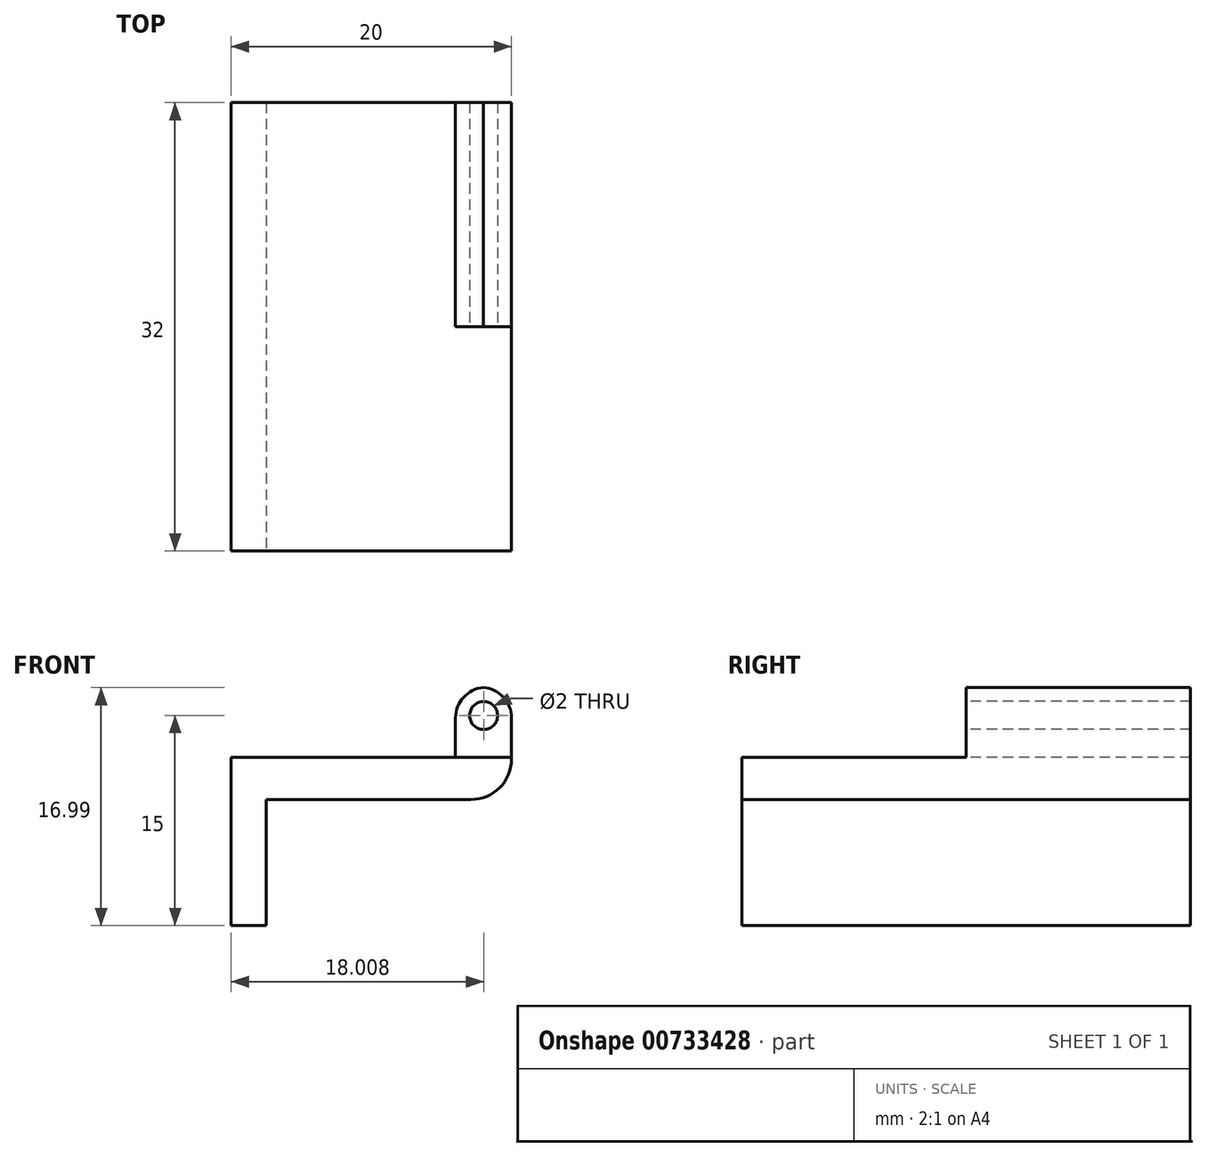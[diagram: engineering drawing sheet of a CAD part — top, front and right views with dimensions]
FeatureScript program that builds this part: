
annotation { "Feature Type Name" : "Feature", "Feature Type Description" : "" }
export const myFeature = defineFeature(function(context is Context, id is Id, definition is map)
    precondition{}
    {
        {
            var Q0;
            Q0=qCreatedBy(makeId("Top.planeOp"),FACE);
            var sketch = newSketch(context, id + "F0", { "sketchPlane" : qUnion([Q0])});
            skLineSegment(sketch, "E0.bottom", {"start": v(0, -16) * mm, "end": v(-20, -16) * mm});
            skLineSegment(sketch, "E0.top", {"start": v(0, 16) * mm, "end": v(-20, 16) * mm});
            skLineSegment(sketch, "E0.left", {"start": v(0, -16) * mm, "end": v(0, 16) * mm});
            skLineSegment(sketch, "E0.right", {"start": v(-20, -16) * mm, "end": v(-20, 16) * mm});
            skSolve(sketch);
        }
        {
            var Q0;
            Q0 = qSketchRegion(id + "F0", true);
            extrude(context, id + "F1", {"entities" : qUnion([Q0]), "depth" : 3 * mm, "offsetDistance" : 25 * mm});
        }
        {
            var Q0;
            Q0=makeQuery(id+"F1.opExtrude","CAP_FACE",FACE,{"disambiguationData":[OSD([sQuery(id+"F0.wireOp",EDGE,"E0.bottom"),sQuery(id+"F0.wireOp",EDGE,"E0.top"),sQuery(id+"F0.wireOp",EDGE,"E0.left"),sQuery(id+"F0.wireOp",EDGE,"E0.right")])],"isStart":true});
            var sketch = newSketch(context, id + "F2", { "sketchPlane" : qUnion([Q0])});
            skLineSegment(sketch, "E1.bottom", {"start": v(-20, -16) * mm, "end": v(-17.5, -16) * mm});
            skLineSegment(sketch, "E1.top", {"start": v(-20, 16) * mm, "end": v(-17.5, 16) * mm});
            skLineSegment(sketch, "E1.left", {"start": v(-20, -16) * mm, "end": v(-20, 16) * mm});
            skLineSegment(sketch, "E1.right", {"start": v(-17.5, -16) * mm, "end": v(-17.5, 16) * mm});
            skSolve(sketch);
        }
        {
            var Q0;
            Q0=makeQuery(id+"F2.imprint","IMPRINT",FACE,{"disambiguationData":[TD([[makeQuery(id+"F2.imprint","IMPRINT",EDGE,{"derivedFrom":sQuery(id+"F2.wireOp",EDGE,"E1.bottom")}),-1.0]])]});
            extrude(context, id + "F3", {"entities" : qUnion([Q0]), "operationType" : NewBodyOperationType.ADD, "depth" : 9 * mm, "offsetDistance" : 25 * mm});
        }
        {
            var Q0;
            Q0=makeQuery(id+"F1.opExtrude","CAP_EDGE",EDGE,{"disambiguationData":[OSD([sQuery(id+"F0.wireOp",EDGE,"E0.left")])],"isStart":true});
            fillet(context, id + "F4", {"entities" : qUnion([Q0]), "radius" : 2.9 * mm, "tangentPropagation" : true, "allowEdgeOverflow" : false});
        }
        {
            var Q0;
            Q0=makeQuery(id+"F1.opExtrude","CAP_FACE",FACE,{"disambiguationData":[OSD([sQuery(id+"F0.wireOp",EDGE,"E0.bottom"),sQuery(id+"F0.wireOp",EDGE,"E0.top"),sQuery(id+"F0.wireOp",EDGE,"E0.left"),sQuery(id+"F0.wireOp",EDGE,"E0.right")])],"isStart":false});
            var sketch = newSketch(context, id + "F5", { "sketchPlane" : qUnion([Q0])});
            skLineSegment(sketch, "E2.bottom", {"start": v(0, 16) * mm, "end": v(0, 16) * mm});
            skLineSegment(sketch, "E2.top", {"start": v(0, 0) * mm, "end": v(0, 0) * mm});
            skLineSegment(sketch, "E2.left", {"start": v(0, 16) * mm, "end": v(0, 0) * mm});
            skLineSegment(sketch, "E2.right", {"start": v(0, 16) * mm, "end": v(0, 0) * mm});
            skLineSegment(sketch, "E3.bottom", {"start": v(0, 16) * mm, "end": v(-4, 16) * mm});
            skLineSegment(sketch, "E3.top", {"start": v(0, 0) * mm, "end": v(-4, 0) * mm});
            skLineSegment(sketch, "E3.right", {"start": v(-4, 16) * mm, "end": v(-4, 0) * mm});
            skSolve(sketch);
        }
        {
            var Q0;
            Q0=makeQuery(id+"F5.imprint","IMPRINT",FACE,{"disambiguationData":[TD([[makeQuery(id+"F5.imprint","IMPRINT",EDGE,{"derivedFrom":sQuery(id+"F5.wireOp",EDGE,"E3.bottom")}),1.0]])]});
            extrude(context, id + "F6", {"entities" : qUnion([Q0]), "operationType" : NewBodyOperationType.ADD, "depth" : 5 * mm, "offsetDistance" : 25 * mm});
        }
        {
            var Q0;
            Q0=makeQuery(id+"F6.opExtrude","SWEPT_FACE",FACE,{"disambiguationData":[OSD([sQuery(id+"F5.wireOp",EDGE,"E3.top")])]});
            var sketch = newSketch(context, id + "F7", { "sketchPlane" : qUnion([Q0])});
            skCircle(sketch, "E4", {"center": v(-2, 6) * mm, "radius": 1 * mm});
            skSolve(sketch);
        }
        {
            var Q0;
            Q0 = qSketchRegion(id + "F7", true);
            extrude(context, id + "F8", {"entities" : qUnion([Q0]), "operationType" : NewBodyOperationType.REMOVE, "oppositeDirection" : true, "depth" : 25 * mm, "offsetDistance" : 25 * mm});
        }
        {
            var Q0;
            Q0=makeQuery(id+"F6.opExtrude","CAP_EDGE",EDGE,{"disambiguationData":[OSD([sQuery(id+"F5.wireOp",EDGE,"E3.right")])],"isStart":false});
            var Q1;
            Q1=makeQuery(id+"F6.opExtrude","CAP_EDGE",EDGE,{"disambiguationData":[OSD([sQuery(id+"F5.wireOp",EDGE,"E2.left")])],"isStart":false});
            fillet(context, id + "F9", {"entities" : qUnion([Q0, Q1]), "radius" : 2.17 * mm, "tangentPropagation" : true, "allowEdgeOverflow" : false});
        }
    });
